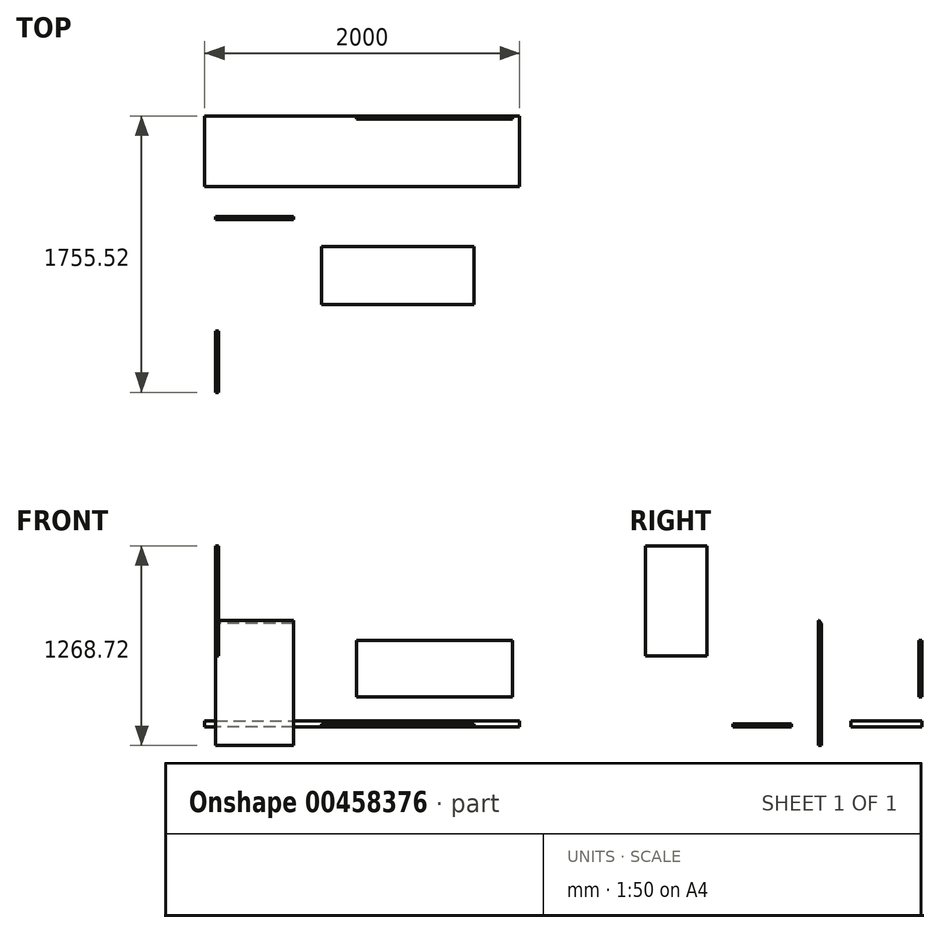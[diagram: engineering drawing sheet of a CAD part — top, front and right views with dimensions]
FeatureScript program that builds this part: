
annotation { "Feature Type Name" : "Feature", "Feature Type Description" : "" }
export const myFeature = defineFeature(function(context is Context, id is Id, definition is map)
    precondition{}
    {
        {
            var Q0;
            Q0=qCreatedBy(makeId("Front.planeOp"),FACE);
            var sketch = newSketch(context, id + "F0", { "sketchPlane" : qUnion([Q0])});
            skLineSegment(sketch, "E0", {"start": v(-69.29, 40) * mm, "end": v(1930.71, 40) * mm});
            skLineSegment(sketch, "E1", {"start": v(1930.71, 40) * mm, "end": v(1930.71, 0) * mm});
            skLineSegment(sketch, "E2", {"start": v(1930.71, 0) * mm, "end": v(-69.29, 0) * mm});
            skLineSegment(sketch, "E3", {"start": v(-69.29, 0) * mm, "end": v(-69.29, 40) * mm});
            skSolve(sketch);
        }
        {
            var Q0;
            Q0=makeQuery(id+"F0.imprint","IMPRINT",FACE,{"disambiguationData":[TD([[makeQuery(id+"F0.imprint","IMPRINT",EDGE,{"derivedFrom":sQuery(id+"F0.wireOp",EDGE,"E0")}),-1.0]])]});
            extrude(context, id + "F1", {"entities" : qUnion([Q0]), "depth" : 450 * mm});
        }
        {
            var Q0;
            Q0=qCreatedBy(makeId("Right.planeOp"),FACE);
            var sketch = newSketch(context, id + "F2", { "sketchPlane" : qUnion([Q0])});
            skLineSegment(sketch, "E4", {"start": v(-658.83, 677.9) * mm, "end": v(-653.83, 677.9) * mm});
            skLineSegment(sketch, "E5", {"start": v(-658.83, 677.9) * mm, "end": v(-658.83, -117.1) * mm});
            skLineSegment(sketch, "E6", {"start": v(-658.83, -117.1) * mm, "end": v(-638.83, -117.1) * mm});
            skLineSegment(sketch, "E7", {"start": v(-638.83, -117.1) * mm, "end": v(-638.83, 657.9) * mm});
            skLineSegment(sketch, "E8", {"start": v(-638.83, 657.9) * mm, "end": v(-653.83, 677.9) * mm});
            skSolve(sketch);
        }
        {
            var Q0;
            Q0 = qSketchRegion(id + "F2", true);
            extrude(context, id + "F3", {"entities" : qUnion([Q0]), "depth" : 495 * mm});
        }
        {
            var Q0;
            Q0=qCreatedBy(makeId("Front.planeOp"),FACE);
            var sketch = newSketch(context, id + "F4", { "sketchPlane" : qUnion([Q0])});
            skLineSegment(sketch, "E9.bottom", {"start": v(895.95, 551.72) * mm, "end": v(1885.95, 551.72) * mm});
            skLineSegment(sketch, "E9.top", {"start": v(895.95, 191.72) * mm, "end": v(1885.95, 191.72) * mm});
            skLineSegment(sketch, "E9.left", {"start": v(895.95, 551.72) * mm, "end": v(895.95, 191.72) * mm});
            skLineSegment(sketch, "E9.right", {"start": v(1885.95, 551.72) * mm, "end": v(1885.95, 191.72) * mm});
            skSolve(sketch);
        }
        {
            var Q0;
            Q0 = qSketchRegion(id + "F4", true);
            var Q1;
            Q1=makeQuery(id+"F4.imprint","IMPRINT",FACE,{"disambiguationData":[TD([[makeQuery(id+"F4.imprint","IMPRINT",EDGE,{"derivedFrom":sQuery(id+"F4.wireOp",EDGE,"E9.bottom")}),-1.0]])]});
            extrude(context, id + "F5", {"entities" : qUnion([Q0, Q1]), "depth" : 20 * mm});
        }
        {
            var Q0;
            Q0=qCreatedBy(makeId("Right.planeOp"),FACE);
            var sketch = newSketch(context, id + "F6", { "sketchPlane" : qUnion([Q0])});
            skLineSegment(sketch, "E10.bottom", {"start": v(-1755.52, 451.63) * mm, "end": v(-1365.52, 451.63) * mm});
            skLineSegment(sketch, "E10.top", {"start": v(-1755.52, 1151.63) * mm, "end": v(-1365.52, 1151.63) * mm});
            skLineSegment(sketch, "E10.left", {"start": v(-1755.52, 451.63) * mm, "end": v(-1755.52, 1151.63) * mm});
            skLineSegment(sketch, "E10.right", {"start": v(-1365.52, 451.63) * mm, "end": v(-1365.52, 1151.63) * mm});
            skSolve(sketch);
        }
        {
            var Q0;
            Q0=makeQuery(id+"F6.imprint","IMPRINT",FACE,{"disambiguationData":[TD([[makeQuery(id+"F6.imprint","IMPRINT",EDGE,{"derivedFrom":sQuery(id+"F6.wireOp",EDGE,"E10.bottom")}),1.0]])]});
            extrude(context, id + "F7", {"entities" : qUnion([Q0]), "depth" : 20 * mm});
        }
        {
            var Q0;
            Q0=qCreatedBy(makeId("Top.planeOp"),FACE);
            var sketch = newSketch(context, id + "F8", { "sketchPlane" : qUnion([Q0])});
            skLineSegment(sketch, "E11.bottom", {"start": v(672.38, -829.1) * mm, "end": v(1642.38, -829.1) * mm});
            skLineSegment(sketch, "E11.top", {"start": v(672.38, -1199.1) * mm, "end": v(1642.38, -1199.1) * mm});
            skLineSegment(sketch, "E11.left", {"start": v(672.38, -829.1) * mm, "end": v(672.38, -1199.1) * mm});
            skLineSegment(sketch, "E11.right", {"start": v(1642.38, -829.1) * mm, "end": v(1642.38, -1199.1) * mm});
            skSolve(sketch);
        }
        {
            var Q0;
            Q0 = qSketchRegion(id + "F8", true);
            extrude(context, id + "F9", {"entities" : qUnion([Q0]), "depth" : 20 * mm});
        }
    });
